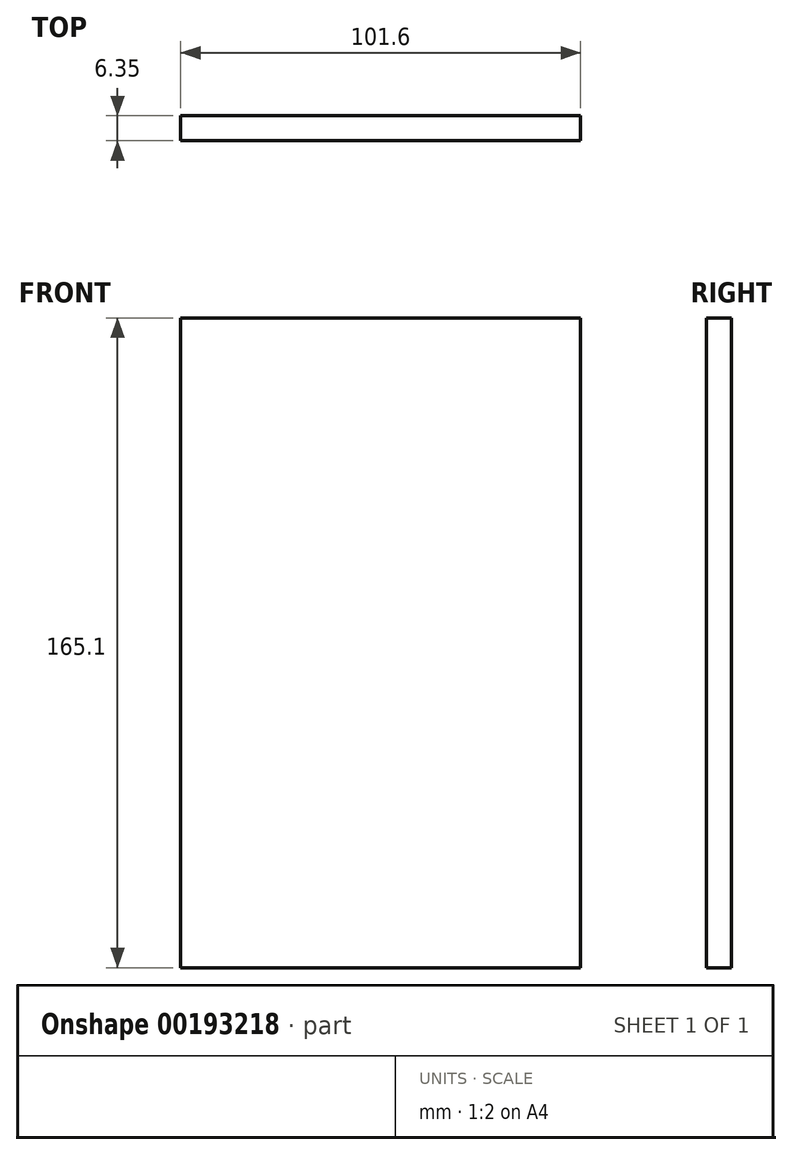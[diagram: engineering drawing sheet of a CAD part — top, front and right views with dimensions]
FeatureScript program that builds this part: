
annotation { "Feature Type Name" : "Feature", "Feature Type Description" : "" }
export const myFeature = defineFeature(function(context is Context, id is Id, definition is map)
    precondition{}
    {
        {
            var Q0;
            Q0=qCreatedBy(makeId("Front.planeOp"),FACE);
            var sketch = newSketch(context, id + "F0", { "sketchPlane" : qUnion([Q0])});
            skLineSegment(sketch, "E0.bottom", {"start": v(-48.12, 36.09) * mm, "end": v(53.48, 36.09) * mm});
            skLineSegment(sketch, "E0.top", {"start": v(-48.12, -129.01) * mm, "end": v(53.48, -129.01) * mm});
            skLineSegment(sketch, "E0.left", {"start": v(-48.12, 36.09) * mm, "end": v(-48.12, -129.01) * mm});
            skLineSegment(sketch, "E0.right", {"start": v(53.48, 36.09) * mm, "end": v(53.48, -129.01) * mm});
            skSolve(sketch);
        }
        {
            var Q0;
            Q0 = qSketchRegion(id + "F0", true);
            extrude(context, id + "F1", {"entities" : qUnion([Q0]), "depth" : 6.35 * mm});
        }
    });
